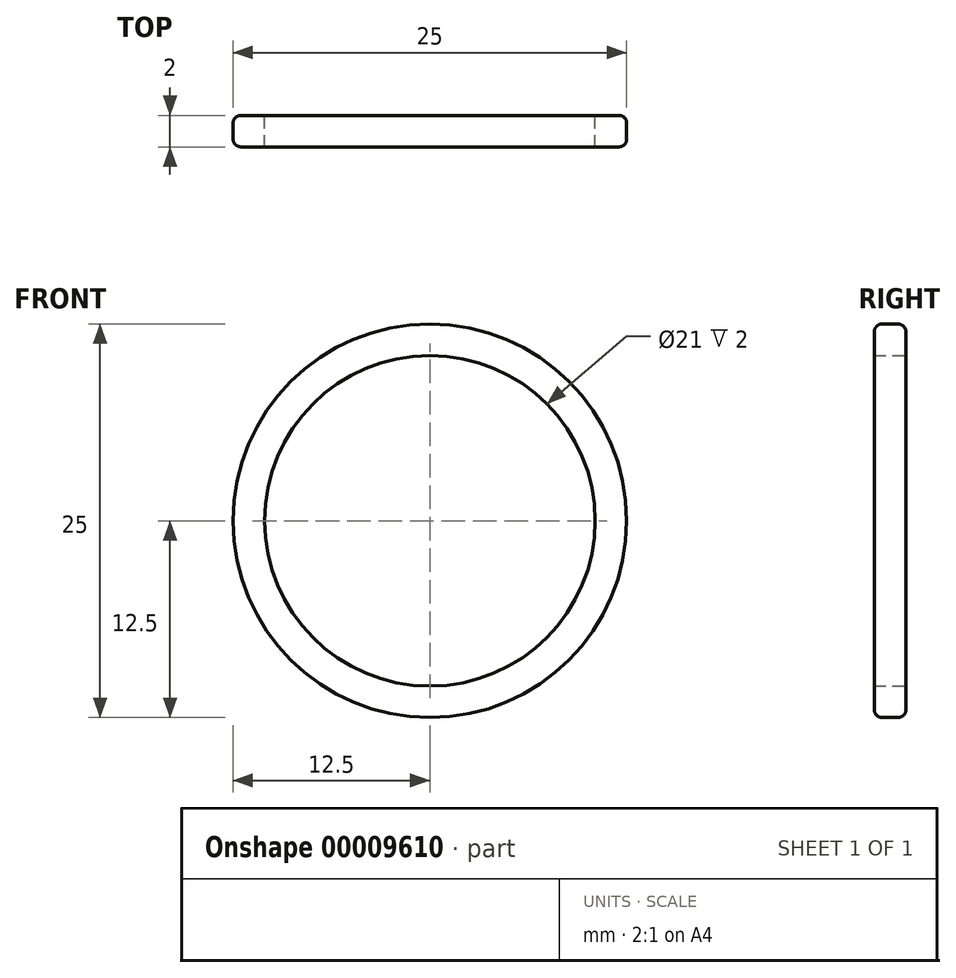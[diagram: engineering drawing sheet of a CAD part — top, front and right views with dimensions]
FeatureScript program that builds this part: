
annotation { "Feature Type Name" : "Feature", "Feature Type Description" : "" }
export const myFeature = defineFeature(function(context is Context, id is Id, definition is map)
    precondition{}
    {
        {
            var Q0;
            Q0=qCreatedBy(makeId("Front.planeOp"),FACE);
            var sketch = newSketch(context, id + "F0", { "sketchPlane" : qUnion([Q0])});
            skCircle(sketch, "E0", {"center": v(0, 0) * mm, "radius": 12.5 * mm});
            skCircle(sketch, "E1", {"center": v(0, 0) * mm, "radius": 10.5 * mm});
            skLineSegment(sketch, "E2", {"start": v(14.11, -12.5) * mm, "end": v(-23.66, -12.5) * mm, "construction": true});
            skSolve(sketch);
        }
        {
            var Q0;
            Q0 = qSketchRegion(id + "F0", true);
            extrude(context, id + "F1", {"entities" : qUnion([Q0]), "depth" : 2 * mm});
        }
        {
            var Q0;
            Q0=makeQuery(id+"F1.opExtrude","CAP_EDGE",EDGE,{"disambiguationData":[OSD([sQuery(id+"F0.wireOp",EDGE,"E0")])],"isStart":false});
            var Q1;
            Q1=makeQuery(id+"F1.opExtrude","CAP_EDGE",EDGE,{"disambiguationData":[OSD([sQuery(id+"F0.wireOp",EDGE,"E0")])],"isStart":true});
            fillet(context, id + "F2", {"entities" : qUnion([Q0, Q1]), "radius" : 0.5 * mm, "tangentPropagation" : true, "allowEdgeOverflow" : false});
        }
        {
            var Q0;
            Q0=qCreatedBy(makeId("Right.planeOp"),FACE);
            var sketch = newSketch(context, id + "F3", { "sketchPlane" : qUnion([Q0])});
            skLineSegment(sketch, "E3", {"start": v(0, -11.5) * mm, "end": v(-2, -11.5) * mm, "construction": true});
            skPoint(sketch, "E4", {"position": v(-1, -11.5) * mm});
            skSolve(sketch);
        }
    });
